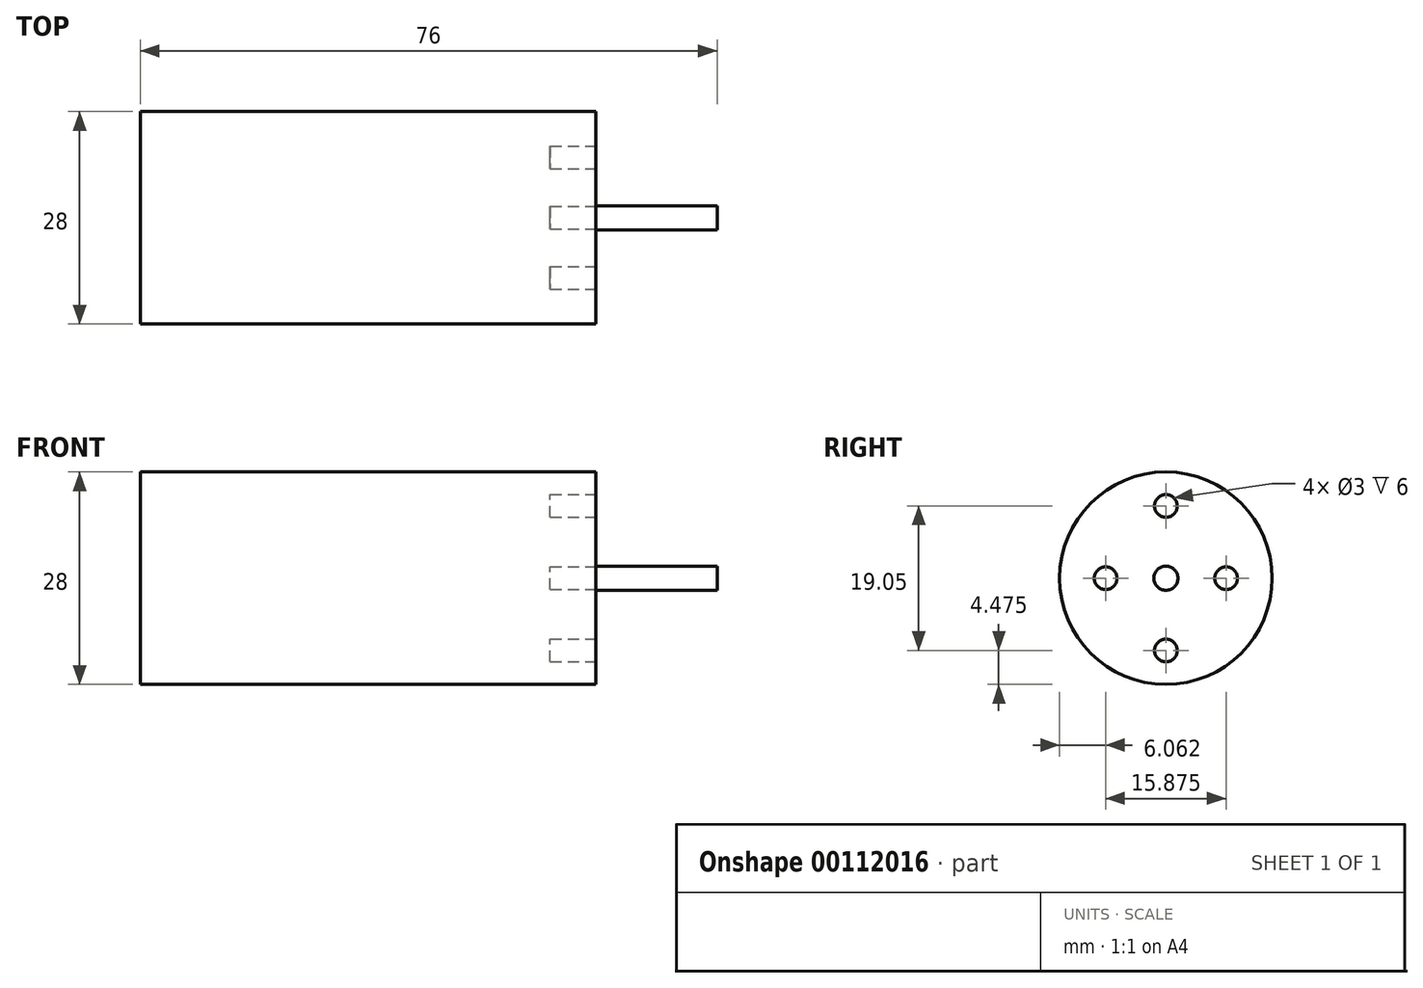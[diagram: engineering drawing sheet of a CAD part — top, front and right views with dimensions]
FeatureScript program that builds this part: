
annotation { "Feature Type Name" : "Feature", "Feature Type Description" : "" }
export const myFeature = defineFeature(function(context is Context, id is Id, definition is map)
    precondition{}
    {
        {
            var Q0;
            Q0=qCreatedBy(makeId("Right.planeOp"),FACE);
            var sketch = newSketch(context, id + "F0", { "sketchPlane" : qUnion([Q0])});
            skCircle(sketch, "E0", {"center": v(0, 0) * mm, "radius": 14 * mm});
            skSolve(sketch);
        }
        {
            var Q0;
            Q0=qSketchRegion(id+"F0",true);
            extrude(context, id + "F1", {"entities" : qUnion([Q0]), "oppositeDirection" : true, "depth" : 60 * mm});
        }
        {
            var Q0;
            Q0=makeQuery(id+"F1.opExtrude","CAP_FACE",FACE,{"disambiguationData":[OSD([sQuery(id+"F0.wireOp",EDGE,"E0")])],"isStart":true});
            var sketch = newSketch(context, id + "F2", { "sketchPlane" : qUnion([Q0])});
            skCircle(sketch, "E1", {"center": v(0, 0) * mm, "radius": 1.59 * mm});
            skSolve(sketch);
        }
        {
            var Q0;
            Q0=qSketchRegion(id+"F2",true);
            extrude(context, id + "F3", {"entities" : qUnion([Q0]), "operationType" : NewBodyOperationType.ADD, "depth" : 16 * mm});
        }
        {
            var Q0;
            Q0=makeQuery(id+"F1.opExtrude","CAP_FACE",FACE,{"disambiguationData":[OSD([sQuery(id+"F0.wireOp",EDGE,"E0")])],"isStart":true});
            var sketch = newSketch(context, id + "F4", { "sketchPlane" : qUnion([Q0])});
            skCircle(sketch, "E2", {"center": v(0, 0) * mm, "radius": 7.94 * mm, "construction": true});
            skCircle(sketch, "E3", {"center": v(0, 0) * mm, "radius": 9.53 * mm, "construction": true});
            skCircle(sketch, "E4", {"center": v(0, 9.53) * mm, "radius": 1.5 * mm});
            skCircle(sketch, "E5", {"center": v(7.94, 0) * mm, "radius": 1.5 * mm});
            skCircle(sketch, "E6", {"center": v(0, -9.53) * mm, "radius": 1.5 * mm});
            skCircle(sketch, "E7", {"center": v(-7.94, 0) * mm, "radius": 1.5 * mm});
            skSolve(sketch);
        }
        {
            var Q0;
            Q0=qSketchRegion(id+"F4",true);
            extrude(context, id + "F5", {"entities" : qUnion([Q0]), "operationType" : NewBodyOperationType.REMOVE, "oppositeDirection" : true, "depth" : 6 * mm});
        }
    });
